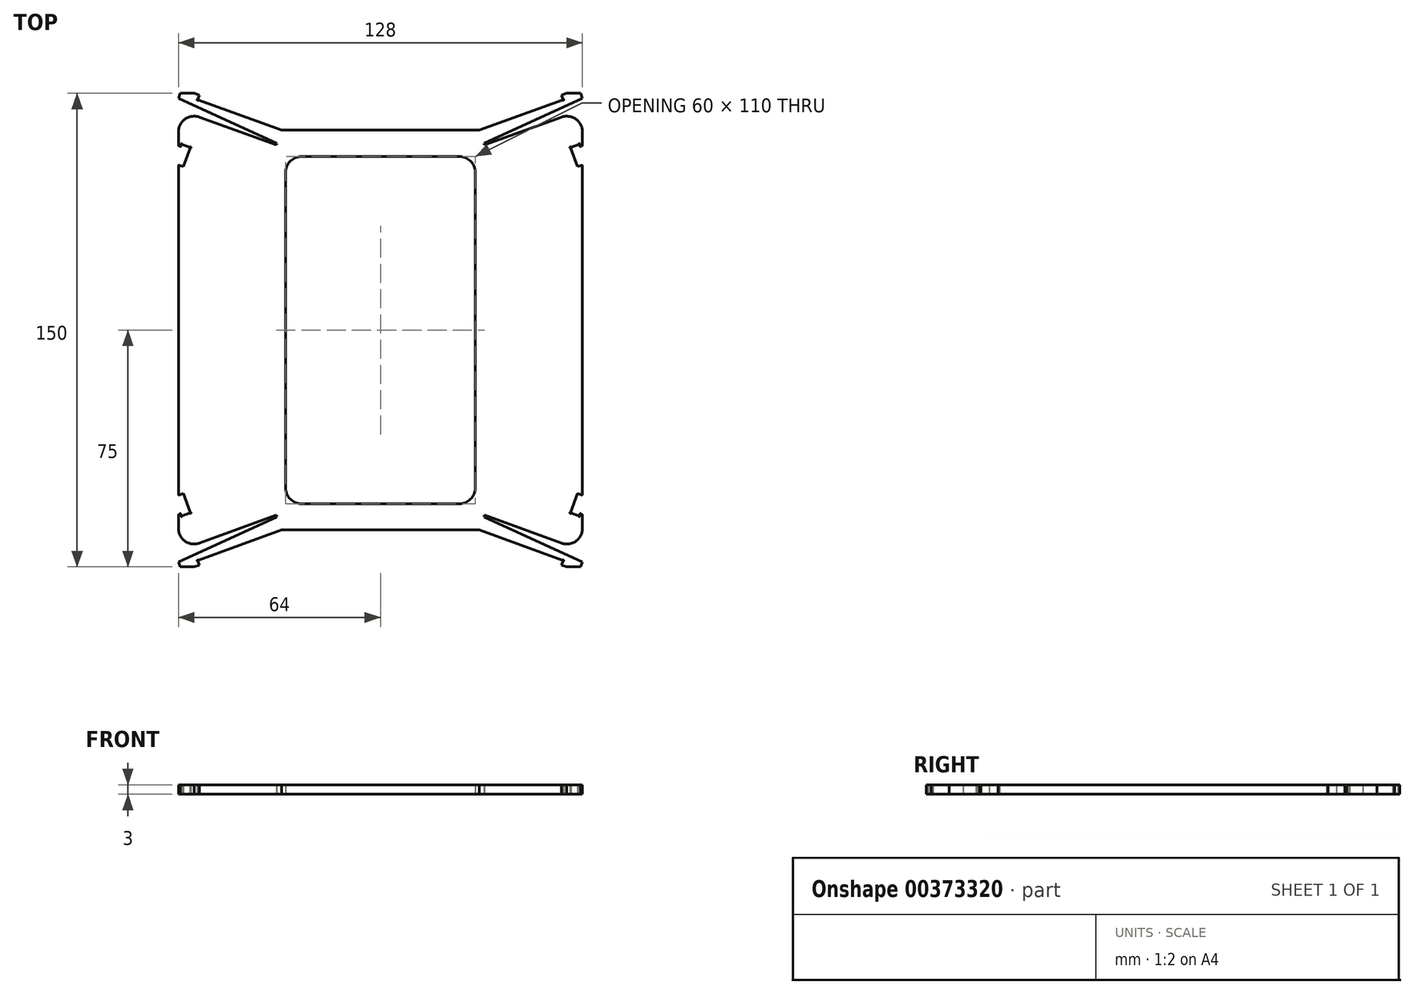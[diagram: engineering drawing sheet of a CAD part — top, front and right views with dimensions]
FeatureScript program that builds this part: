
annotation { "Feature Type Name" : "Feature", "Feature Type Description" : "" }
export const myFeature = defineFeature(function(context is Context, id is Id, definition is map)
    precondition{}
    {
        {
            var Q0;
            Q0=qCreatedBy(makeId("Top.planeOp"),FACE);
            var sketch = newSketch(context, id + "F0", { "sketchPlane" : qUnion([Q0])});
            skLineSegment(sketch, "E0", {"start": v(0, 63.3) * mm, "end": v(0, 0) * mm});
            skLineSegment(sketch, "E1", {"start": v(0, 0) * mm, "end": v(64, 0) * mm});
            skLineSegment(sketch, "E2.top", {"start": v(64, 69.9) * mm, "end": v(33, 58.6) * mm});
            skLineSegment(sketch, "E2.right", {"start": v(31.28, 63.3) * mm, "end": v(33, 58.6) * mm, "construction": true});
            skLineSegment(sketch, "E3.bottom", {"start": v(60.18, 57.86) * mm, "end": v(63, 58.89) * mm});
            skLineSegment(sketch, "E3.top", {"start": v(62.4, 51.75) * mm, "end": v(63.73, 52.24) * mm});
            skLineSegment(sketch, "E3.left", {"start": v(60.18, 57.86) * mm, "end": v(62.4, 51.75) * mm});
            skLineSegment(sketch, "E4.top", {"start": v(63.93, 58.44) * mm, "end": v(63.56, 58.13) * mm});
            skLineSegment(sketch, "E4.right", {"start": v(63, 58.89) * mm, "end": v(63.24, 58.21) * mm});
            skArc(sketch, "E5", {"start": v(60.37, 57.93) * mm, "mid": v(60, 57.94) * mm, "end": v(60.25, 57.67) * mm});
            skLineSegment(sketch, "E6", {"start": v(31.28, 63.3) * mm, "end": v(0, 63.3) * mm});
            skLineSegment(sketch, "E7", {"start": v(64, 69.9) * mm, "end": v(64, 58.6) * mm});
            skLineSegment(sketch, "E8", {"start": v(31.28, 63.3) * mm, "end": v(57.87, 72.98) * mm});
            skLineSegment(sketch, "E9", {"start": v(57.87, 72.98) * mm, "end": v(57.36, 74.4) * mm});
            skLineSegment(sketch, "E10", {"start": v(57.36, 74.4) * mm, "end": v(59.03, 75) * mm});
            skLineSegment(sketch, "E11", {"start": v(59.03, 75) * mm, "end": v(63.42, 75) * mm});
            skLineSegment(sketch, "E12", {"start": v(63.42, 75) * mm, "end": v(64, 73.4) * mm});
            skLineSegment(sketch, "E13", {"start": v(64, 73.4) * mm, "end": v(32.78, 59.17) * mm});
            skLineSegment(sketch, "E14", {"start": v(64, 52.05) * mm, "end": v(64, 0) * mm});
            skArc(sketch, "E15", {"start": v(62.81, 58.82) * mm, "mid": v(63.08, 59.07) * mm, "end": v(63.07, 58.7) * mm});
            skPoint(sketch, "E16.visualSharp", {"position": v(64, 58.5) * mm});
            skArc(sketch, "E16.filletArc", {"start": v(63.93, 58.44) * mm, "mid": v(63.98, 58.5) * mm, "end": v(64, 58.6) * mm});
            skPoint(sketch, "E17.visualSharp", {"position": v(63.34, 57.95) * mm});
            skArc(sketch, "E17.filletArc", {"start": v(63.24, 58.21) * mm, "mid": v(63.38, 58.09) * mm, "end": v(63.56, 58.13) * mm});
            skPoint(sketch, "E18.visualSharp", {"position": v(64, 52.33) * mm});
            skArc(sketch, "E18.filletArc", {"start": v(64, 52.05) * mm, "mid": v(63.91, 52.21) * mm, "end": v(63.73, 52.24) * mm});
            skArc(sketch, "E19", {"start": v(57.78, 73.16) * mm, "mid": v(58.06, 72.9) * mm, "end": v(57.68, 72.91) * mm});
            skLineSegment(sketch, "E20", {"start": v(32.78, 59.17) * mm, "end": v(33, 58.6) * mm});
            skSolve(sketch);
        }
        {
            var Q0;
            Q0=makeQuery(id+"F0.imprint","IMPRINT",FACE,{"disambiguationData":[TD([[makeQuery(id+"F0.imprint","IMPRINT",EDGE,{"derivedFrom":sQuery(id+"F0.wireOp",EDGE,"cINau8Vk-rqU0-VEj9-B1Ag-C2JGWQrqNEj4")}),-1.0]])]});
            var Q1;
            {var subQ1=sQuery(id+"F0.wireOp",EDGE,"E4.top");Q1=makeQuery(id+"F0.imprint","IMPRINT",FACE,{"disambiguationData":[TD([[makeQuery(id+"F0.imprint","IMPRINT",EDGE,{"derivedFrom":subQ1}),-1.0]])]});}
            extrude(context, id + "F1", {"entities" : qUnion([Q0, Q1]), "endBound" : BoundingType.SYMMETRIC, "depth" : 3 * mm});
        }
        {
            var Q0;
            Q0=makeQuery(id+"F1.opExtrude","SWEPT_BODY",BODY,{"disambiguationData":[OSD([sQuery(id+"F0.wireOp",EDGE,"cINau8Vk-rqU0-VEj9-B1Ag-C2JGWQrqNEj4"),sQuery(id+"F0.wireOp",EDGE,"335dc9dd-e92c-45d7-9ed7-1d2665347acc"),sQuery(id+"F0.wireOp",EDGE,"70a021d9-a8ba-4676-9a3f-a5b4aa380b94"),sQuery(id+"F0.wireOp",EDGE,"18f37769-42f8-4c2d-90dc-6550737fb793"),sQuery(id+"F0.wireOp",EDGE,"3da6a0b3-34a3-4880-8a49-8ff13df7a461"),sQuery(id+"F0.wireOp",EDGE,"f828dd15-c4d8-4cba-8546-9f8a7f9381f5"),sQuery(id+"F0.wireOp",EDGE,"a91f05f4-a340-49a0-a8b6-4c85a1d15d21"),sQuery(id+"F0.wireOp",EDGE,"9af4c470-1a3b-4441-9bc9-09c286b1daf9"),sQuery(id+"F0.wireOp",EDGE,"79c36709-ff2b-4bac-8a45-15eb8bf69461"),sQuery(id+"F0.wireOp",EDGE,"6d08cd5a-1224-4490-81af-2cd0a7e8aec6.bottom"),sQuery(id+"F0.wireOp",EDGE,"6d08cd5a-1224-4490-81af-2cd0a7e8aec6.top"),sQuery(id+"F0.wireOp",EDGE,"6d08cd5a-1224-4490-81af-2cd0a7e8aec6.left"),sQuery(id+"F0.wireOp",EDGE,"6d08cd5a-1224-4490-81af-2cd0a7e8aec6.right"),sQuery(id+"F0.wireOp",EDGE,"58a87e60-b25b-4d61-8558-b00d63ac34c1"),sQuery(id+"F0.wireOp",EDGE,"6b1f11f5-8e9c-46f7-a1d9-19e2294995c0"),sQuery(id+"F0.wireOp",EDGE,"602494c9-f376-467d-8326-49e4208fd98d.MirrorCS"),sQuery(id+"F0.wireOp",EDGE,"49953555-be9f-4ffe-a27f-7c7e93abad84.MirrorCS"),sQuery(id+"F0.wireOp",EDGE,"8cef824f-6fe9-4cd6-8e02-8374a151b543.MirrorCS"),sQuery(id+"F0.wireOp",EDGE,"7680e948-62e6-4be4-bf34-3076eed9468e.MirrorCS"),sQuery(id+"F0.wireOp",EDGE,"73c64eb1-9053-4ded-a230-a61976290448.MirrorCS"),sQuery(id+"F0.wireOp",EDGE,"46b4f519-7eed-4a56-a145-91be8fb33702.MirrorCS"),sQuery(id+"F0.wireOp",EDGE,"afc91494-e45a-4e0d-8478-c1c4b8668b17.MirrorCS"),sQuery(id+"F0.wireOp",EDGE,"7f78c9ac-dab3-470e-b2fd-83acb2de593e.MirrorCS"),sQuery(id+"F0.wireOp",EDGE,"fd935eb7-e968-4ba5-b237-c59b83bfb19d.MirrorCS"),sQuery(id+"F0.wireOp",EDGE,"f2f82a07-4409-4f8e-8d96-87c223b0c0d3.MirrorCS"),sQuery(id+"F0.wireOp",EDGE,"d213cde9-c748-450c-b3ab-b43775edb233.MirrorCS"),sQuery(id+"F0.wireOp",EDGE,"ad376563-d176-4530-9e5c-6096e98fd02a.MirrorCS"),sQuery(id+"F0.wireOp",EDGE,"10c4e4fb-938e-455d-a0e2-646973584c52.MirrorCS"),sQuery(id+"F0.wireOp",EDGE,"4cbfe46b-0b7b-4cb7-ba8e-9a60a7c1606d.MirrorCS"),sQuery(id+"F0.wireOp",EDGE,"0670d096-9497-4416-bedd-0344c1049003.MirrorCS"),sQuery(id+"F0.wireOp",EDGE,"72b22dc0-100e-4d8f-8d39-dd5216eacbb7"),sQuery(id+"F0.wireOp",EDGE,"238d3171-18cf-4664-875a-15b81accc3c9"),sQuery(id+"F0.wireOp",EDGE,"7124a334-57a5-4c12-b1ba-874bc8632110.MirrorC"),sQuery(id+"F0.wireOp",EDGE,"41e78b87-379c-4209-bddd-e93b811ec0c7"),sQuery(id+"F0.wireOp",EDGE,"44bece61-ac72-4aae-9b04-1ec5777349d3"),sQuery(id+"F0.wireOp",EDGE,"E0"),sQuery(id+"F0.wireOp",EDGE,"E1")])]});
            var Q1;
            Q1=makeQuery(id+"F1.opExtrude","SWEPT_FACE",FACE,{"disambiguationData":[OSD([sQuery(id+"F0.wireOp",EDGE,"E0")])]});
            mirror(context, id + "F2", {"operationType" : NewBodyOperationType.ADD, "entities" : qUnion([Q0]), "mirrorPlane" : qUnion([Q1])});
        }
        {
            var Q0;
            Q0=makeQuery(id+"F1.opExtrude","SWEPT_BODY",BODY,{"disambiguationData":[OSD([sQuery(id+"F0.wireOp",EDGE,"cINau8Vk-rqU0-VEj9-B1Ag-C2JGWQrqNEj4"),sQuery(id+"F0.wireOp",EDGE,"335dc9dd-e92c-45d7-9ed7-1d2665347acc"),sQuery(id+"F0.wireOp",EDGE,"70a021d9-a8ba-4676-9a3f-a5b4aa380b94"),sQuery(id+"F0.wireOp",EDGE,"18f37769-42f8-4c2d-90dc-6550737fb793"),sQuery(id+"F0.wireOp",EDGE,"3da6a0b3-34a3-4880-8a49-8ff13df7a461"),sQuery(id+"F0.wireOp",EDGE,"f828dd15-c4d8-4cba-8546-9f8a7f9381f5"),sQuery(id+"F0.wireOp",EDGE,"a91f05f4-a340-49a0-a8b6-4c85a1d15d21"),sQuery(id+"F0.wireOp",EDGE,"9af4c470-1a3b-4441-9bc9-09c286b1daf9"),sQuery(id+"F0.wireOp",EDGE,"79c36709-ff2b-4bac-8a45-15eb8bf69461"),sQuery(id+"F0.wireOp",EDGE,"6d08cd5a-1224-4490-81af-2cd0a7e8aec6.bottom"),sQuery(id+"F0.wireOp",EDGE,"6d08cd5a-1224-4490-81af-2cd0a7e8aec6.top"),sQuery(id+"F0.wireOp",EDGE,"6d08cd5a-1224-4490-81af-2cd0a7e8aec6.left"),sQuery(id+"F0.wireOp",EDGE,"6d08cd5a-1224-4490-81af-2cd0a7e8aec6.right"),sQuery(id+"F0.wireOp",EDGE,"58a87e60-b25b-4d61-8558-b00d63ac34c1"),sQuery(id+"F0.wireOp",EDGE,"6b1f11f5-8e9c-46f7-a1d9-19e2294995c0"),sQuery(id+"F0.wireOp",EDGE,"602494c9-f376-467d-8326-49e4208fd98d.MirrorCS"),sQuery(id+"F0.wireOp",EDGE,"49953555-be9f-4ffe-a27f-7c7e93abad84.MirrorCS"),sQuery(id+"F0.wireOp",EDGE,"8cef824f-6fe9-4cd6-8e02-8374a151b543.MirrorCS"),sQuery(id+"F0.wireOp",EDGE,"7680e948-62e6-4be4-bf34-3076eed9468e.MirrorCS"),sQuery(id+"F0.wireOp",EDGE,"73c64eb1-9053-4ded-a230-a61976290448.MirrorCS"),sQuery(id+"F0.wireOp",EDGE,"46b4f519-7eed-4a56-a145-91be8fb33702.MirrorCS"),sQuery(id+"F0.wireOp",EDGE,"afc91494-e45a-4e0d-8478-c1c4b8668b17.MirrorCS"),sQuery(id+"F0.wireOp",EDGE,"7f78c9ac-dab3-470e-b2fd-83acb2de593e.MirrorCS"),sQuery(id+"F0.wireOp",EDGE,"fd935eb7-e968-4ba5-b237-c59b83bfb19d.MirrorCS"),sQuery(id+"F0.wireOp",EDGE,"f2f82a07-4409-4f8e-8d96-87c223b0c0d3.MirrorCS"),sQuery(id+"F0.wireOp",EDGE,"d213cde9-c748-450c-b3ab-b43775edb233.MirrorCS"),sQuery(id+"F0.wireOp",EDGE,"ad376563-d176-4530-9e5c-6096e98fd02a.MirrorCS"),sQuery(id+"F0.wireOp",EDGE,"10c4e4fb-938e-455d-a0e2-646973584c52.MirrorCS"),sQuery(id+"F0.wireOp",EDGE,"4cbfe46b-0b7b-4cb7-ba8e-9a60a7c1606d.MirrorCS"),sQuery(id+"F0.wireOp",EDGE,"0670d096-9497-4416-bedd-0344c1049003.MirrorCS"),sQuery(id+"F0.wireOp",EDGE,"72b22dc0-100e-4d8f-8d39-dd5216eacbb7"),sQuery(id+"F0.wireOp",EDGE,"238d3171-18cf-4664-875a-15b81accc3c9"),sQuery(id+"F0.wireOp",EDGE,"7124a334-57a5-4c12-b1ba-874bc8632110.MirrorC"),sQuery(id+"F0.wireOp",EDGE,"41e78b87-379c-4209-bddd-e93b811ec0c7"),sQuery(id+"F0.wireOp",EDGE,"44bece61-ac72-4aae-9b04-1ec5777349d3"),sQuery(id+"F0.wireOp",EDGE,"E0"),sQuery(id+"F0.wireOp",EDGE,"E1")])]});
            var Q1;
            {var subQ0=makeQuery(id+"F1.opExtrude","SWEPT_FACE",FACE,{"disambiguationData":[OSD([sQuery(id+"F0.wireOp",EDGE,"E1")])]});Q1=makeQuery(id+"F2.boolean.opBoolean","MERGE",FACE,{"derivedFrom":[subQ0,makeQuery(id+"F2.opPattern","COPY",FACE,{"derivedFrom":subQ0,"instanceName":"1"})]});}
            mirror(context, id + "F3", {"operationType" : NewBodyOperationType.ADD, "entities" : qUnion([Q0]), "mirrorPlane" : qUnion([Q1])});
        }
        {
            var Q0;
            {var subQ0=makeQuery(id+"F1.opExtrude","CAP_FACE",FACE,{"disambiguationData":[OSD([sQuery(id+"F0.wireOp",EDGE,"E0"),sQuery(id+"F0.wireOp",EDGE,"E1"),sQuery(id+"F0.wireOp",EDGE,"E2.top"),sQuery(id+"F0.wireOp",EDGE,"E3.bottom"),sQuery(id+"F0.wireOp",EDGE,"E3.top"),sQuery(id+"F0.wireOp",EDGE,"E3.left"),sQuery(id+"F0.wireOp",EDGE,"E4.top"),sQuery(id+"F0.wireOp",EDGE,"E4.right"),sQuery(id+"F0.wireOp",EDGE,"E5"),sQuery(id+"F0.wireOp",EDGE,"E6"),sQuery(id+"F0.wireOp",EDGE,"E7"),sQuery(id+"F0.wireOp",EDGE,"E8"),sQuery(id+"F0.wireOp",EDGE,"E9"),sQuery(id+"F0.wireOp",EDGE,"E10"),sQuery(id+"F0.wireOp",EDGE,"E11"),sQuery(id+"F0.wireOp",EDGE,"E12"),sQuery(id+"F0.wireOp",EDGE,"E13"),sQuery(id+"F0.wireOp",EDGE,"E14"),sQuery(id+"F0.wireOp",EDGE,"E15"),sQuery(id+"F0.wireOp",EDGE,"E16.filletArc"),sQuery(id+"F0.wireOp",EDGE,"E17.filletArc"),sQuery(id+"F0.wireOp",EDGE,"E18.filletArc"),sQuery(id+"F0.wireOp",EDGE,"E19"),sQuery(id+"F0.wireOp",EDGE,"E20")])],"isStart":true});var subQ1=makeQuery(id+"F2.boolean.opBoolean","MERGE",FACE,{"derivedFrom":[subQ0,makeQuery(id+"F2.opPattern","COPY",FACE,{"derivedFrom":subQ0,"instanceName":"1"})]});Q0=makeQuery(id+"F3.boolean.opBoolean","MERGE",FACE,{"derivedFrom":[subQ1,makeQuery(id+"F3.opPattern","COPY",FACE,{"derivedFrom":subQ1,"instanceName":"1"})]});}
            var sketch = newSketch(context, id + "F4", { "sketchPlane" : qUnion([Q0])});
            skLineSegment(sketch, "E21.bottom", {"start": v(30, 55) * mm, "end": v(-30, 55) * mm});
            skLineSegment(sketch, "E21.top", {"start": v(30, -55) * mm, "end": v(-30, -55) * mm});
            skLineSegment(sketch, "E21.left", {"start": v(30, 55) * mm, "end": v(30, -55) * mm});
            skLineSegment(sketch, "E21.right", {"start": v(-30, 55) * mm, "end": v(-30, -55) * mm});
            skPoint(sketch, "E21.middle", {"position": v(0, 0) * mm});
            skSolve(sketch);
        }
        {
            var Q0;
            Q0 = qSketchRegion(id + "F4", true);
            var Q1;
            {var subQ0=makeQuery(id+"F1.opExtrude","CAP_FACE",FACE,{"disambiguationData":[OSD([sQuery(id+"F0.wireOp",EDGE,"E0"),sQuery(id+"F0.wireOp",EDGE,"E1"),sQuery(id+"F0.wireOp",EDGE,"E2.top"),sQuery(id+"F0.wireOp",EDGE,"E3.bottom"),sQuery(id+"F0.wireOp",EDGE,"E3.top"),sQuery(id+"F0.wireOp",EDGE,"E3.left"),sQuery(id+"F0.wireOp",EDGE,"E4.top"),sQuery(id+"F0.wireOp",EDGE,"E4.right"),sQuery(id+"F0.wireOp",EDGE,"E5"),sQuery(id+"F0.wireOp",EDGE,"E6"),sQuery(id+"F0.wireOp",EDGE,"E7"),sQuery(id+"F0.wireOp",EDGE,"E8"),sQuery(id+"F0.wireOp",EDGE,"E9"),sQuery(id+"F0.wireOp",EDGE,"E10"),sQuery(id+"F0.wireOp",EDGE,"E11"),sQuery(id+"F0.wireOp",EDGE,"E12"),sQuery(id+"F0.wireOp",EDGE,"E13"),sQuery(id+"F0.wireOp",EDGE,"E14"),sQuery(id+"F0.wireOp",EDGE,"E15"),sQuery(id+"F0.wireOp",EDGE,"E16.filletArc"),sQuery(id+"F0.wireOp",EDGE,"E17.filletArc"),sQuery(id+"F0.wireOp",EDGE,"E18.filletArc"),sQuery(id+"F0.wireOp",EDGE,"E19"),sQuery(id+"F0.wireOp",EDGE,"E20")])],"isStart":false});var subQ1=makeQuery(id+"F2.boolean.opBoolean","MERGE",FACE,{"derivedFrom":[subQ0,makeQuery(id+"F2.opPattern","COPY",FACE,{"derivedFrom":subQ0,"instanceName":"1"})]});Q1=makeQuery(id+"F3.boolean.opBoolean","MERGE",FACE,{"derivedFrom":[subQ1,makeQuery(id+"F3.opPattern","COPY",FACE,{"derivedFrom":subQ1,"instanceName":"1"})]});}
            extrude(context, id + "F5", {"entities" : qUnion([Q0]), "operationType" : NewBodyOperationType.REMOVE, "endBound" : BoundingType.UP_TO_SURFACE, "oppositeDirection" : true, "endBoundEntityFace" : qUnion([Q1]), "depth" : 25 * mm});
        }
        {
            var Q0;
            Q0=makeQuery(id+"F3.opPattern","COPY",EDGE,{"derivedFrom":makeQuery(id+"F2.opPattern","COPY",EDGE,{"derivedFrom":makeQuery(id+"F1.opExtrude","SWEPT_EDGE",EDGE,{"disambiguationData":[OSD([sQuery(id+"F0.wireOp",EDGE,"E2.top"),sQuery(id+"F0.wireOp",EDGE,"E7")])]}),"instanceName":"1"}),"instanceName":"1"});
            var Q1;
            Q1=makeQuery(id+"F3.opPattern","COPY",EDGE,{"derivedFrom":makeQuery(id+"F1.opExtrude","SWEPT_EDGE",EDGE,{"disambiguationData":[OSD([sQuery(id+"F0.wireOp",EDGE,"E2.top"),sQuery(id+"F0.wireOp",EDGE,"E7")])]}),"instanceName":"1"});
            var Q2;
            Q2=makeQuery(id+"F1.opExtrude","SWEPT_EDGE",EDGE,{"disambiguationData":[OSD([sQuery(id+"F0.wireOp",EDGE,"E2.top"),sQuery(id+"F0.wireOp",EDGE,"E7")])]});
            var Q3;
            Q3=makeQuery(id+"F2.opPattern","COPY",EDGE,{"derivedFrom":makeQuery(id+"F1.opExtrude","SWEPT_EDGE",EDGE,{"disambiguationData":[OSD([sQuery(id+"F0.wireOp",EDGE,"E2.top"),sQuery(id+"F0.wireOp",EDGE,"E7")])]}),"instanceName":"1"});
            fillet(context, id + "F6", {"entities" : qUnion([Q0, Q1, Q2, Q3]), "radius" : 5 * mm, "tangentPropagation" : true, "allowEdgeOverflow" : false});
        }
        {
            var Q0;
            Q0=makeQuery(id+"F5.boolean.opBoolean","COPY",EDGE,{"derivedFrom":makeQuery(id+"F5.opExtrude","SWEPT_EDGE",EDGE,{"disambiguationData":[OSD([sQuery(id+"F4.wireOp",EDGE,"E21.top"),sQuery(id+"F4.wireOp",EDGE,"E21.right")])]})});
            var Q1;
            Q1=makeQuery(id+"F5.boolean.opBoolean","COPY",EDGE,{"derivedFrom":makeQuery(id+"F5.opExtrude","SWEPT_EDGE",EDGE,{"disambiguationData":[OSD([sQuery(id+"F4.wireOp",EDGE,"E21.bottom"),sQuery(id+"F4.wireOp",EDGE,"E21.right")])]})});
            var Q2;
            Q2=makeQuery(id+"F5.boolean.opBoolean","COPY",EDGE,{"derivedFrom":makeQuery(id+"F5.opExtrude","SWEPT_EDGE",EDGE,{"disambiguationData":[OSD([sQuery(id+"F4.wireOp",EDGE,"E21.bottom"),sQuery(id+"F4.wireOp",EDGE,"E21.left")])]})});
            var Q3;
            Q3=makeQuery(id+"F5.boolean.opBoolean","COPY",EDGE,{"derivedFrom":makeQuery(id+"F5.opExtrude","SWEPT_EDGE",EDGE,{"disambiguationData":[OSD([sQuery(id+"F4.wireOp",EDGE,"E21.top"),sQuery(id+"F4.wireOp",EDGE,"E21.left")])]})});
            fillet(context, id + "F7", {"entities" : qUnion([Q0, Q1, Q2, Q3]), "radius" : 5 * mm, "tangentPropagation" : true, "allowEdgeOverflow" : false});
        }
    });
